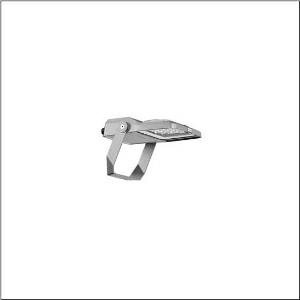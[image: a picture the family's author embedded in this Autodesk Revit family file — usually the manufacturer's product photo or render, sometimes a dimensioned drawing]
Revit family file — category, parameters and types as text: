
# Revit family: floodlight_fl_21_iq_micro___rsd12_5xa7762a4b1a_7d54
name_source: partatom
category: Lighting Fixtures
units: mm (PartAtom-declared; Revit-internal decimal feet)

## family parameters
Cut with Voids When Loaded = No
Host = Face
Light Source = No
Part Type = Normal
Room Calculation Point = No
Round Connector Dimension = Use Diameter
Shared = No

## types (1)
- --- (1 x LED, 3220 lm, 23.1 W, 4000K)
    Apparent Load = 23 VA
    CIE Flux Codes = 79 92 99 100 100
    Color Rendering = 70
    Color Temperature = 4000K
    Default Elevation = 1800 mm
    Description = Floodlight FL 21 iQ micro, floodlight, primary light control with lens, of PMMA, primary optical cover: protective disc, of toughened safety glass, transparent, light distribution: RSD12, light emission: direct distribution, installation type: surface-mounted, lamps: LED, High Power LED, rated values: 3.220lm | 23,1W | 139,4lm/W (begin service life); end service life: 3.220lm | 23,8W; at 50% lumin. flux: 1.610lm | 11W | 146,4lm/W, colour temperature: 4000K, colour rendering: CRI > 70, light colour: 740, light setting 1 begin service life: 100% | 3.220lm | 23,1W | 139,4lm/W | 4.000K, light setting 1 end service life: 23,8W, further light settings possible, control: Auto-Match, Temp-Guard, Night-Set, Smart-Wire, Desk-Remote (wireless, voltage-free reading and setting of iQ features in the workshop via application-optimized NFC function/RFID function), optimised constant luminous flux control (CLO 2.0), Street-Remote, pre-setting: linear dimming characteristic, with terminal, 6-pole, mains connection: 220..240V, AC, 50/60Hz, luminaire housing, of diecast aluminium, powder-coated, SITECO metallic grey (DB 702S), corrosivity category C5 mid according to DIN EN ISO 12944suitable for swimming poolschlorine-resistant, sealing non-destructively replaceable, mounting bracket, of steel, galvanised, powder-coated, SITECO metallic grey (DB 702S), protection rating (complete): IP66, insulation class (complete): insulation class II (safety insulation), certification: CE, ENEC, VDE, protection symbol: D, impact resistance: IK07, permissible operating ambient temperature: -40..+40°C, permissible operating ambient temperature for outdoor applications: -40..+50°C, standard: DIN EN 12944, LABS conformity tested according to VDMA 24364:2018-05, packaging unit: 1 piece

Light Distribution: RSD12
    Height = 65 mm
    Lamp = 1 x LED
    Lamp Light Flux = 3220 lm
    Lamp Power = 23.1 W
    Lamp count = 1
    Length = 312 mm
    Luminous efficacy = 139 lm/W
    Manufacturer = Siteco
    ModVariant = No
    Model = 5XA7762A4B1A
    Mounting Place = Wall
    Mounting Type = Surface mounted
    Number of Poles = 1
    OnlyDefault = Yes
    Power Factor = 1
    Product Name = Floodlight FL 21 iQ micro | RSD12
    Product group = floodlight | wall mounted
    ProductGroupID = 2002
    Protection Class = Protection class II
    Protection Degree = IP 66
    RLX_Detail_Level = 1
    RLX_Emergency_Light_Flux = 0 lm
    RLX_Emergency_Type = 0
    RLX_Emergency_Type_DB = No
    RlxData = <blob elided: 75193 chars, md5=bbd14880>
    Socket = socket
    Standby Power = 0 W
    System Light Flux = 3220 lm
    System Power = 23 W
    Type Comments = factory setting: luminous flux: 100 % | dim-lin: 254 | 455 mA
    Type Image = l_1006880.jpg
    URL = http://relux.com
    VarID = @adj_179713
    Voltage = 0 V
    Weight = 0.00 kg
    Width = 230 mm

## geometry (parser evidence)
native form markers: Blend x4, Sweep x13
no freeform markers — native parametric forms only
